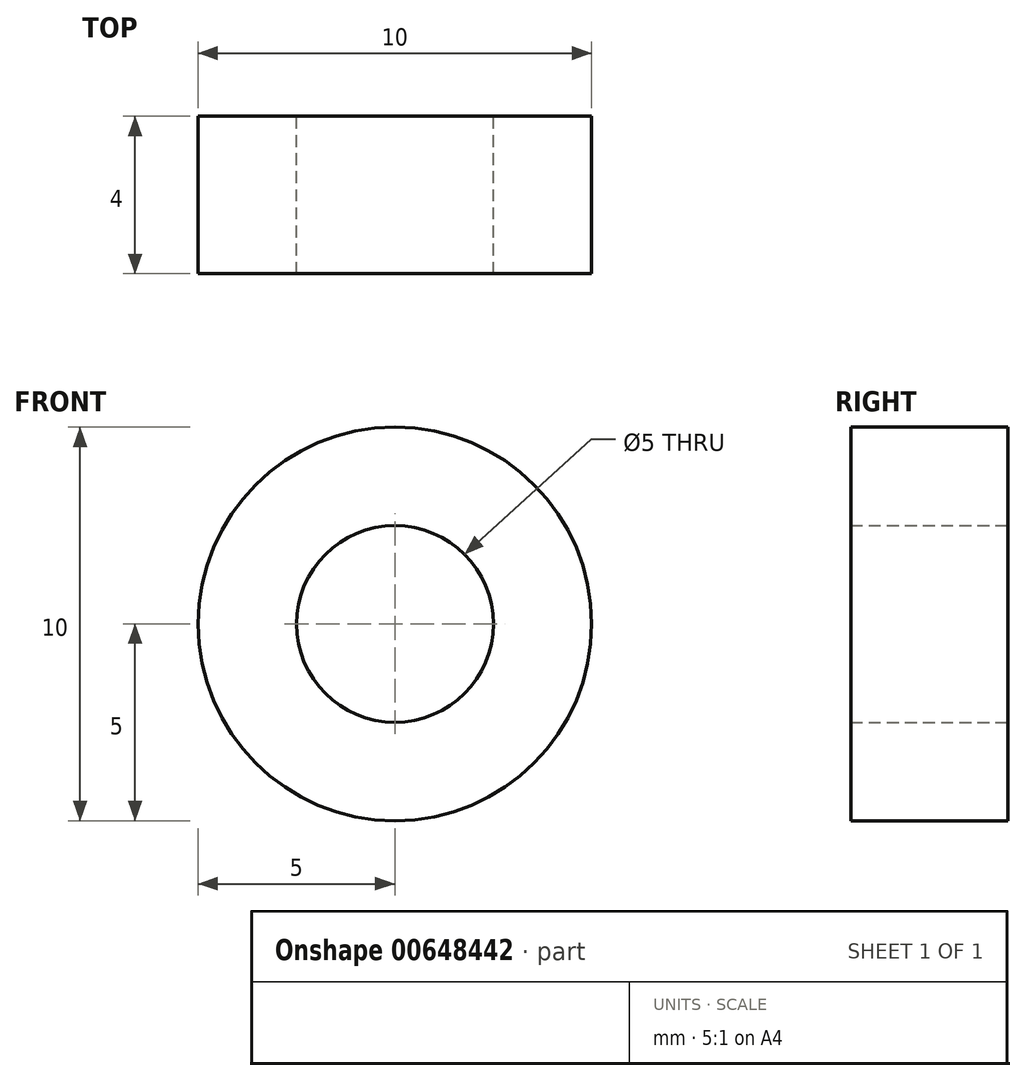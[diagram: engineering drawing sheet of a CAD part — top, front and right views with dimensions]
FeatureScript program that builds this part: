
annotation { "Feature Type Name" : "Feature", "Feature Type Description" : "" }
export const myFeature = defineFeature(function(context is Context, id is Id, definition is map)
    precondition{}
    {
        {
            var Q0;
            Q0=qCreatedBy(makeId("Front.planeOp"),FACE);
            var sketch = newSketch(context, id + "F0", { "sketchPlane" : qUnion([Q0])});
            skCircle(sketch, "E0", {"center": v(0, 0) * mm, "radius": 5 * mm});
            skCircle(sketch, "E1", {"center": v(0, 0) * mm, "radius": 2.5 * mm});
            skSolve(sketch);
        }
        {
            var Q0;
            Q0=makeQuery(id+"F0.imprint","IMPRINT",FACE,{"disambiguationData":[TD([[makeQuery(id+"F0.imprint","IMPRINT",EDGE,{"derivedFrom":sQuery(id+"F0.wireOp",EDGE,"E0")}),1.0]])]});
            extrude(context, id + "F1", {"entities" : qUnion([Q0]), "depth" : 4 * mm});
        }
    });
